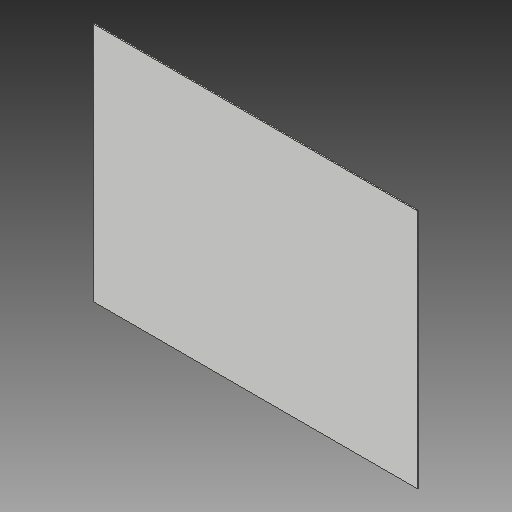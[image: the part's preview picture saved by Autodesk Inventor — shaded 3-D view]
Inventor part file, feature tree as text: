
AUTODESK INVENTOR PART (.ipt)
format: ipt  version: 2017 (Build 210142000, 142)  size: 83,968 bytes
history: native  units: in
note: dims shown in document units (in); Inventor stores cm internally (conversion verified against a paired STEP export)
features: extrude x1, sketch x1
ambient origin geometry x8: Origin, YZ Plane, XZ Plane, XY Plane, X Axis, Y Axis, Z Axis, Center Point
bodies: Solid1 (feature_tree)
feature tree (2):
  extrude  "Extrusion1"  Depth=13.0in
  sketch  "Sketch1"  dims[d0=17.5in d1=13.0in d2=0.0625in d3=0.0in]
